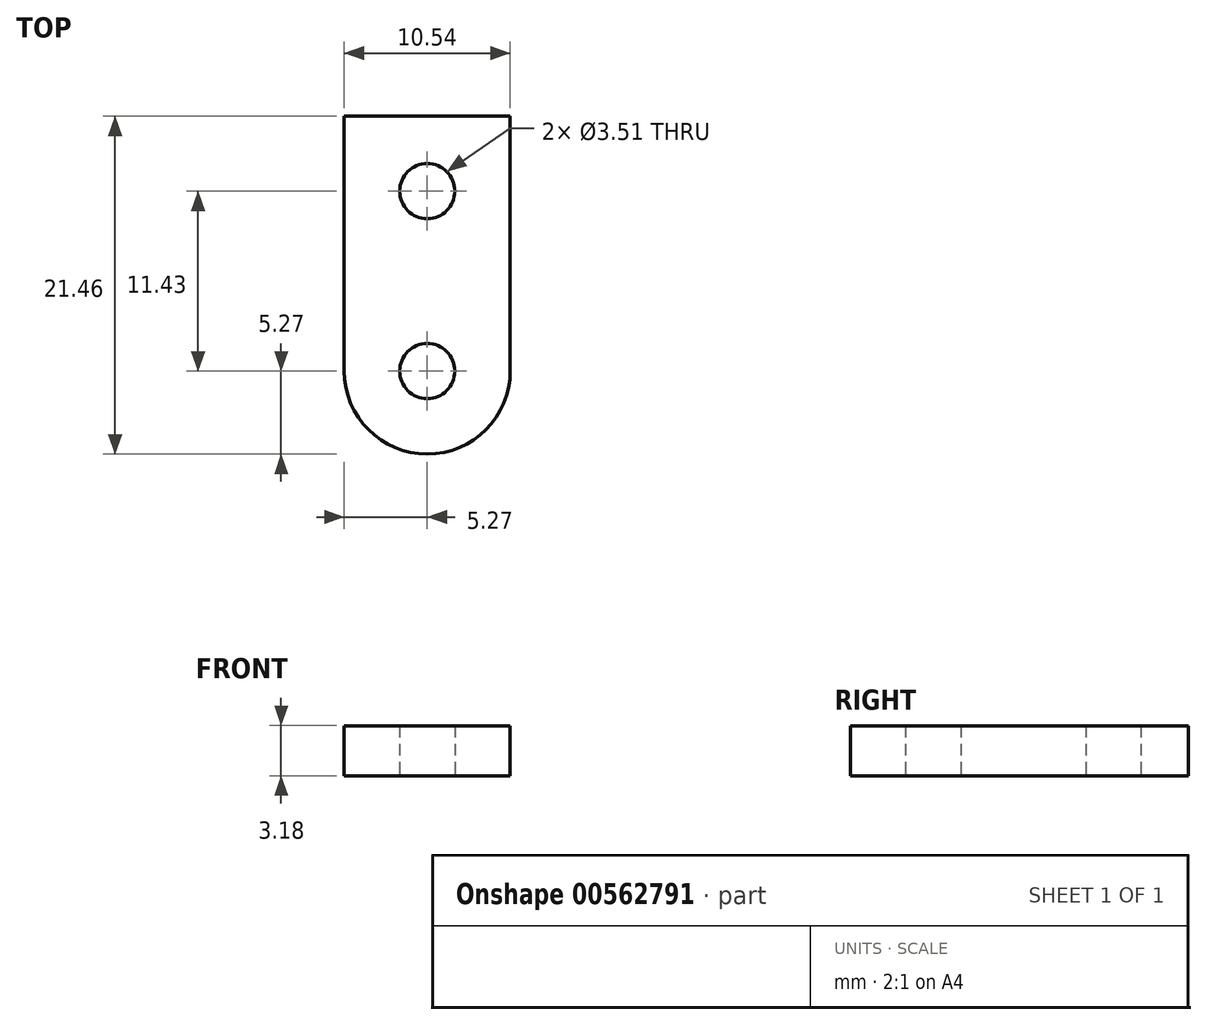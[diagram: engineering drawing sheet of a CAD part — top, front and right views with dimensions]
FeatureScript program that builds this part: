
annotation { "Feature Type Name" : "Feature", "Feature Type Description" : "" }
export const myFeature = defineFeature(function(context is Context, id is Id, definition is map)
    precondition{}
    {
        {
            var Q0;
            Q0=qCreatedBy(makeId("Top.planeOp"),FACE);
            var sketch = newSketch(context, id + "F0", { "sketchPlane" : qUnion([Q0])});
            skLineSegment(sketch, "E0.bottom", {"start": v(-11.11, 3.17) * mm, "end": v(-5.27, 3.17) * mm});
            skLineSegment(sketch, "E0.top", {"start": v(-11.11, -3.18) * mm, "end": v(-5.27, -3.18) * mm});
            skLineSegment(sketch, "E0.left", {"start": v(-11.11, 3.17) * mm, "end": v(-11.11, -3.18) * mm});
            skLineSegment(sketch, "E0.right", {"start": v(11.11, 3.17) * mm, "end": v(11.11, -3.18) * mm});
            skPoint(sketch, "E0.middle", {"position": v(0, 0) * mm});
            skLineSegment(sketch, "E1.top", {"start": v(-5.27, 4.76) * mm, "end": v(5.27, 4.76) * mm});
            skLineSegment(sketch, "E1.left", {"start": v(-5.27, 3.17) * mm, "end": v(-5.27, 4.76) * mm});
            skLineSegment(sketch, "E1.right", {"start": v(5.27, 3.17) * mm, "end": v(5.27, 4.76) * mm});
            skPoint(sketch, "E1.middle", {"position": v(0, 3.97) * mm});
            skLineSegment(sketch, "E2.trimOffspring", {"start": v(5.27, 3.17) * mm, "end": v(11.11, 3.17) * mm});
            skLineSegment(sketch, "E3.MirrorCS", {"start": v(5.27, -3.17) * mm, "end": v(5.27, -4.76) * mm});
            skLineSegment(sketch, "E4.MirrorCS", {"start": v(-5.27, -3.17) * mm, "end": v(-5.27, -4.76) * mm});
            skPoint(sketch, "E5.MirrorP", {"position": v(0, -3.97) * mm});
            skLineSegment(sketch, "E6.MirrorCS", {"start": v(-5.27, -4.76) * mm, "end": v(5.27, -4.76) * mm});
            skLineSegment(sketch, "E7.trimOffspring", {"start": v(5.27, -3.18) * mm, "end": v(11.11, -3.18) * mm});
            skSolve(sketch);
        }
        {
            var Q0;
            Q0=qSketchRegion(id+"F0",true);
            extrude(context, id + "F1", {"entities" : qUnion([Q0]), "depth" : 3.17 * mm, "offsetDistance" : 25.4 * mm});
        }
        {
            var Q0;
            Q0=makeQuery(id+"F1.opExtrude","CAP_FACE",FACE,{"disambiguationData":[OSD([sQuery(id+"F0.wireOp",EDGE,"E0.bottom"),sQuery(id+"F0.wireOp",EDGE,"E0.top"),sQuery(id+"F0.wireOp",EDGE,"E0.left"),sQuery(id+"F0.wireOp",EDGE,"E0.right"),sQuery(id+"F0.wireOp",EDGE,"E1.top"),sQuery(id+"F0.wireOp",EDGE,"E1.left"),sQuery(id+"F0.wireOp",EDGE,"E1.right"),sQuery(id+"F0.wireOp",EDGE,"E2.trimOffspring"),sQuery(id+"F0.wireOp",EDGE,"E3.MirrorCS"),sQuery(id+"F0.wireOp",EDGE,"E4.MirrorCS"),sQuery(id+"F0.wireOp",EDGE,"E6.MirrorCS"),sQuery(id+"F0.wireOp",EDGE,"E7.trimOffspring")])],"isStart":true});
            var sketch = newSketch(context, id + "F2", { "sketchPlane" : qUnion([Q0])});
            skCircle(sketch, "E8", {"center": v(0, 11.43) * mm, "radius": 1.75 * mm});
            skArc(sketch, "E9", {"start": v(5.27, 11.43) * mm, "mid": v(0, 16.7) * mm, "end": v(-5.27, 11.43) * mm});
            skLineSegment(sketch, "E10", {"start": v(-5.27, 4.76) * mm, "end": v(-5.27, 11.43) * mm});
            skLineSegment(sketch, "E11", {"start": v(-5.27, 4.76) * mm, "end": v(5.27, 4.76) * mm});
            skLineSegment(sketch, "E12.MirrorCS", {"start": v(5.27, 4.76) * mm, "end": v(5.27, 11.43) * mm});
            skSolve(sketch);
        }
        {
            var Q0;
            Q0=qSketchRegion(id+"F2",true);
            var Q1;
            Q1=makeQuery(id+"F1.opExtrude","CAP_FACE",FACE,{"disambiguationData":[OSD([sQuery(id+"F0.wireOp",EDGE,"E0.bottom"),sQuery(id+"F0.wireOp",EDGE,"E0.top"),sQuery(id+"F0.wireOp",EDGE,"E0.left"),sQuery(id+"F0.wireOp",EDGE,"E0.right"),sQuery(id+"F0.wireOp",EDGE,"E1.top"),sQuery(id+"F0.wireOp",EDGE,"E1.left"),sQuery(id+"F0.wireOp",EDGE,"E1.right"),sQuery(id+"F0.wireOp",EDGE,"E2.trimOffspring"),sQuery(id+"F0.wireOp",EDGE,"E3.MirrorCS"),sQuery(id+"F0.wireOp",EDGE,"E4.MirrorCS"),sQuery(id+"F0.wireOp",EDGE,"E6.MirrorCS"),sQuery(id+"F0.wireOp",EDGE,"E7.trimOffspring")])],"isStart":false});
            extrude(context, id + "F3", {"entities" : qUnion([Q0]), "operationType" : NewBodyOperationType.ADD, "endBound" : BoundingType.UP_TO_SURFACE, "oppositeDirection" : true, "depth" : 25.4 * mm, "endBoundEntityFace" : qUnion([Q1]), "offsetDistance" : 25.4 * mm});
        }
        {
            var Q0;
            Q0=makeQuery(id+"F3.boolean.opBoolean","MERGE",FACE,{"derivedFrom":[makeQuery(id+"F1.opExtrude","CAP_FACE",FACE,{"disambiguationData":[OSD([sQuery(id+"F0.wireOp",EDGE,"E0.bottom"),sQuery(id+"F0.wireOp",EDGE,"E0.top"),sQuery(id+"F0.wireOp",EDGE,"E0.left"),sQuery(id+"F0.wireOp",EDGE,"E0.right"),sQuery(id+"F0.wireOp",EDGE,"E1.top"),sQuery(id+"F0.wireOp",EDGE,"E1.left"),sQuery(id+"F0.wireOp",EDGE,"E1.right"),sQuery(id+"F0.wireOp",EDGE,"E2.trimOffspring"),sQuery(id+"F0.wireOp",EDGE,"E3.MirrorCS"),sQuery(id+"F0.wireOp",EDGE,"E4.MirrorCS"),sQuery(id+"F0.wireOp",EDGE,"E6.MirrorCS"),sQuery(id+"F0.wireOp",EDGE,"E7.trimOffspring")])],"isStart":true}),makeQuery(id+"F3.opExtrude","CAP_FACE",FACE,{"disambiguationData":[OSD([sQuery(id+"F2.wireOp",EDGE,"E8"),sQuery(id+"F2.wireOp",EDGE,"E9"),sQuery(id+"F2.wireOp",EDGE,"E10"),sQuery(id+"F2.wireOp",EDGE,"E11"),sQuery(id+"F2.wireOp",EDGE,"E12.MirrorCS")])],"isStart":true})]});
            var sketch = newSketch(context, id + "F4", { "sketchPlane" : qUnion([Q0])});
            skCircle(sketch, "E13", {"center": v(0, 0) * mm, "radius": 1.75 * mm});
            skSolve(sketch);
        }
        {
            var Q0;
            Q0=qSketchRegion(id+"F4",true);
            extrude(context, id + "F5", {"entities" : qUnion([Q0]), "operationType" : NewBodyOperationType.REMOVE, "oppositeDirection" : true, "depth" : 25.4 * mm, "offsetDistance" : 25.4 * mm});
        }
        {
            var Q0;
            {var subQ0=sQuery(id+"F0.wireOp",EDGE,"E7.trimOffspring");var subQ1=sQuery(id+"F0.wireOp",EDGE,"E6.MirrorCS");var subQ2=sQuery(id+"F0.wireOp",EDGE,"E4.MirrorCS");var subQ3=sQuery(id+"F0.wireOp",EDGE,"E3.MirrorCS");var subQ4=sQuery(id+"F0.wireOp",EDGE,"E2.trimOffspring");var subQ5=sQuery(id+"F0.wireOp",EDGE,"E1.right");var subQ6=sQuery(id+"F0.wireOp",EDGE,"E1.left");var subQ7=sQuery(id+"F0.wireOp",EDGE,"E1.top");var subQ8=sQuery(id+"F0.wireOp",EDGE,"E0.right");var subQ9=sQuery(id+"F0.wireOp",EDGE,"E0.left");var subQ10=sQuery(id+"F0.wireOp",EDGE,"E0.top");var subQ11=sQuery(id+"F0.wireOp",EDGE,"E0.bottom");Q0=makeQuery(id+"F3.boolean.opBoolean","MERGE",FACE,{"derivedFrom":[makeQuery(id+"F1.opExtrude","CAP_FACE",FACE,{"disambiguationData":[OSD([subQ11,subQ10,subQ9,subQ8,subQ7,subQ6,subQ5,subQ4,subQ3,subQ2,subQ1,subQ0])],"isStart":false}),makeQuery(id+"F3.opExtrude","CAP_FACE",FACE,{"disambiguationData":[OSD([subQ11,subQ10,subQ9,subQ8,subQ7,subQ6,subQ5,subQ4,subQ3,subQ2,subQ1,subQ0])],"isStart":false})]});}
            var sketch = newSketch(context, id + "F6", { "sketchPlane" : qUnion([Q0])});
            skLineSegment(sketch, "E14.bottom", {"start": v(-11.11, 3.17) * mm, "end": v(-5.27, 3.17) * mm});
            skLineSegment(sketch, "E14.top", {"start": v(-11.11, -3.18) * mm, "end": v(-5.27, -3.18) * mm});
            skLineSegment(sketch, "E14.left", {"start": v(-11.11, 3.17) * mm, "end": v(-11.11, -3.18) * mm});
            skLineSegment(sketch, "E14.right", {"start": v(-5.27, 3.17) * mm, "end": v(-5.27, -3.18) * mm});
            skLineSegment(sketch, "E15.bottom", {"start": v(11.11, 3.17) * mm, "end": v(5.27, 3.17) * mm});
            skLineSegment(sketch, "E15.top", {"start": v(11.11, -3.17) * mm, "end": v(5.27, -3.17) * mm});
            skLineSegment(sketch, "E15.left", {"start": v(11.11, 3.17) * mm, "end": v(11.11, -3.17) * mm});
            skLineSegment(sketch, "E15.right", {"start": v(5.27, 3.17) * mm, "end": v(5.27, -3.17) * mm});
            skSolve(sketch);
        }
        {
            var Q0;
            Q0 = qSketchRegion(id + "F6", true);
            extrude(context, id + "F7", {"entities" : qUnion([Q0]), "operationType" : NewBodyOperationType.REMOVE, "oppositeDirection" : true, "depth" : 25.4 * mm, "offsetDistance" : 25.4 * mm});
        }
    });
